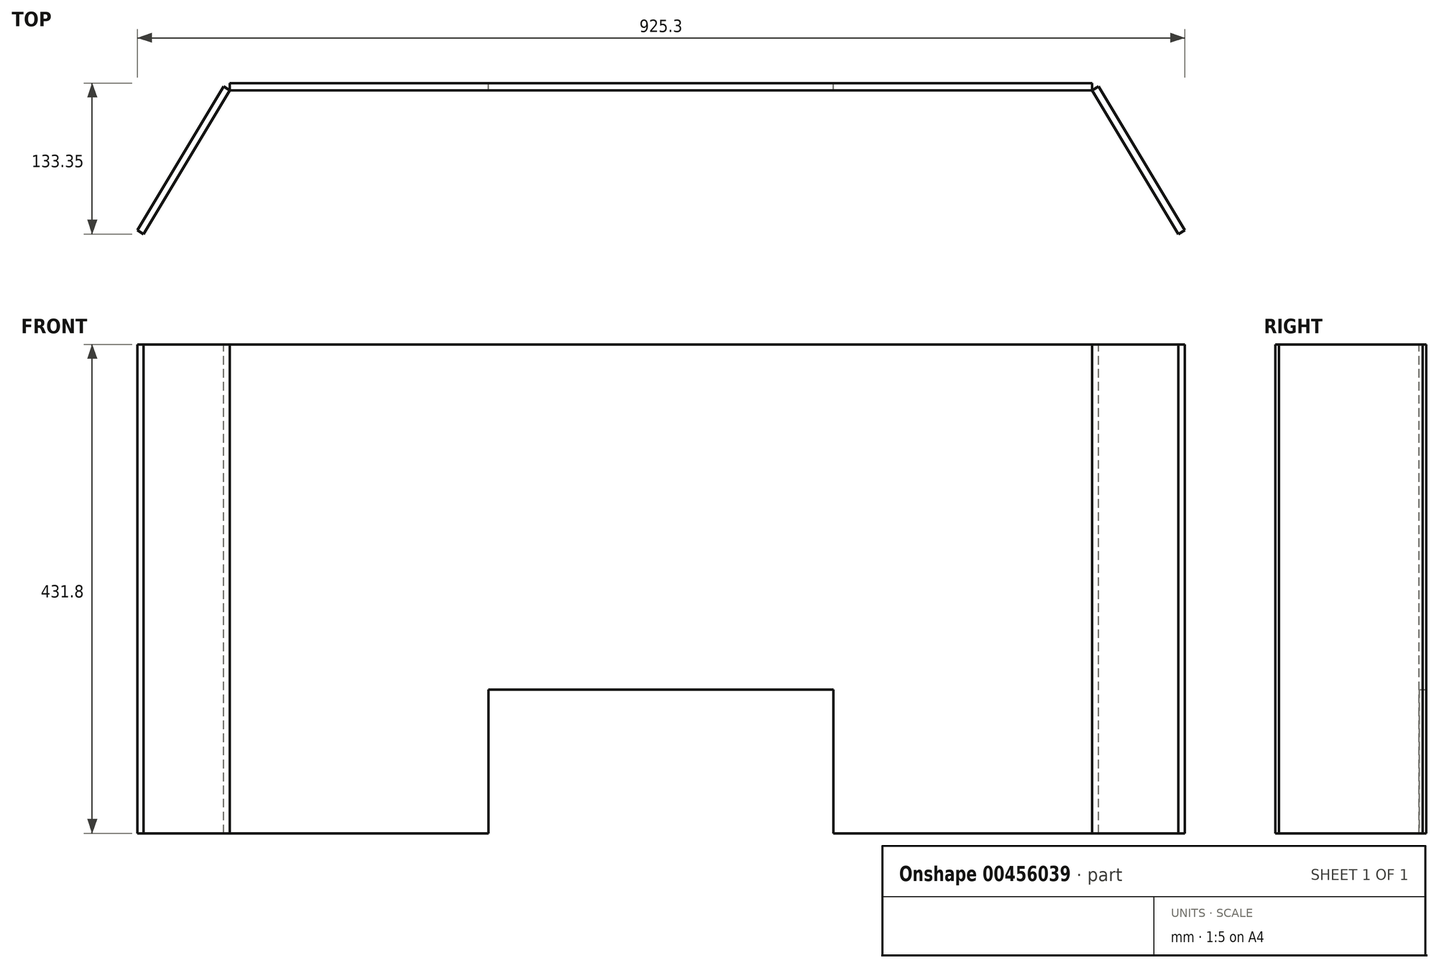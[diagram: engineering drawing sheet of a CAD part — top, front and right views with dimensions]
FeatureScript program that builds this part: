
annotation { "Feature Type Name" : "Feature", "Feature Type Description" : "" }
export const myFeature = defineFeature(function(context is Context, id is Id, definition is map)
    precondition{}
    {
        {
            var Q0;
            Q0=qCreatedBy(makeId("Front.planeOp"),FACE);
            var sketch = newSketch(context, id + "F0", { "sketchPlane" : qUnion([Q0])});
            skLineSegment(sketch, "E0.bottom", {"start": v(0, 0) * mm, "end": v(-762, 0) * mm});
            skLineSegment(sketch, "E0.top", {"start": v(0, -431.8) * mm, "end": v(-228.6, -431.8) * mm});
            skLineSegment(sketch, "E0.left", {"start": v(0, 0) * mm, "end": v(0, -431.8) * mm});
            skLineSegment(sketch, "E0.right", {"start": v(-762, 0) * mm, "end": v(-762, -431.8) * mm});
            skLineSegment(sketch, "E1.right", {"start": v(-228.6, -431.8) * mm, "end": v(-228.6, -304.8) * mm});
            skLineSegment(sketch, "E2.bottom", {"start": v(-228.6, -304.8) * mm, "end": v(-533.4, -304.8) * mm});
            skLineSegment(sketch, "E2.right", {"start": v(-533.4, -304.8) * mm, "end": v(-533.4, -431.8) * mm});
            skPoint(sketch, "E2.top.start.orphan", {"position": v(-228.6, -431.8) * mm});
            skLineSegment(sketch, "E3.trimOffspring", {"start": v(-533.4, -431.8) * mm, "end": v(-762, -431.8) * mm});
            skSolve(sketch);
        }
        {
            var Q0;
            Q0 = qSketchRegion(id + "F0", true);
            extrude(context, id + "F1", {"entities" : qUnion([Q0]), "depth" : 6.35 * mm});
        }
        {
            var Q0;
            Q0=qCreatedBy(makeId("Top.planeOp"),FACE);
            var sketch = newSketch(context, id + "F2", { "sketchPlane" : qUnion([Q0])});
            skLineSegment(sketch, "E4.left", {"start": v(0, 0) * mm, "end": v(0, -6.35) * mm});
            skLineSegment(sketch, "E5", {"start": v(0, -6.35) * mm, "end": v(76.2, -133.35) * mm});
            skLineSegment(sketch, "E6", {"start": v(76.2, -133.35) * mm, "end": v(81.65, -130.08) * mm});
            skLineSegment(sketch, "E7", {"start": v(81.65, -130.08) * mm, "end": v(5.45, -3.08) * mm});
            skLineSegment(sketch, "E8", {"start": v(5.45, -3.08) * mm, "end": v(0, -6.35) * mm});
            skLineSegment(sketch, "E9", {"start": v(0, -6.35) * mm, "end": v(7.4, -6.35) * mm});
            skPoint(sketch, "E10.orphan", {"position": v(76.2, -6.35) * mm});
            skSolve(sketch);
        }
        {
            var Q0;
            Q0 = qSketchRegion(id + "F2", true);
            extrude(context, id + "F3", {"entities" : qUnion([Q0]), "oppositeDirection" : true, "depth" : 431.8 * mm});
        }
        {
            var Q0;
            Q0=qCreatedBy(makeId("Top.planeOp"),FACE);
            var sketch = newSketch(context, id + "F4", { "sketchPlane" : qUnion([Q0])});
            skLineSegment(sketch, "E11", {"start": v(-762, -6.35) * mm, "end": v(-838.2, -133.35) * mm});
            skLineSegment(sketch, "E12", {"start": v(-838.2, -133.35) * mm, "end": v(-843.65, -130.08) * mm});
            skLineSegment(sketch, "E13", {"start": v(-843.65, -130.08) * mm, "end": v(-767.45, -3.08) * mm});
            skLineSegment(sketch, "E14", {"start": v(-767.45, -3.08) * mm, "end": v(-762, -6.35) * mm});
            skSolve(sketch);
        }
        {
            var Q0;
            Q0 = qSketchRegion(id + "F4", true);
            extrude(context, id + "F5", {"entities" : qUnion([Q0]), "oppositeDirection" : true, "depth" : 431.8 * mm});
        }
    });
